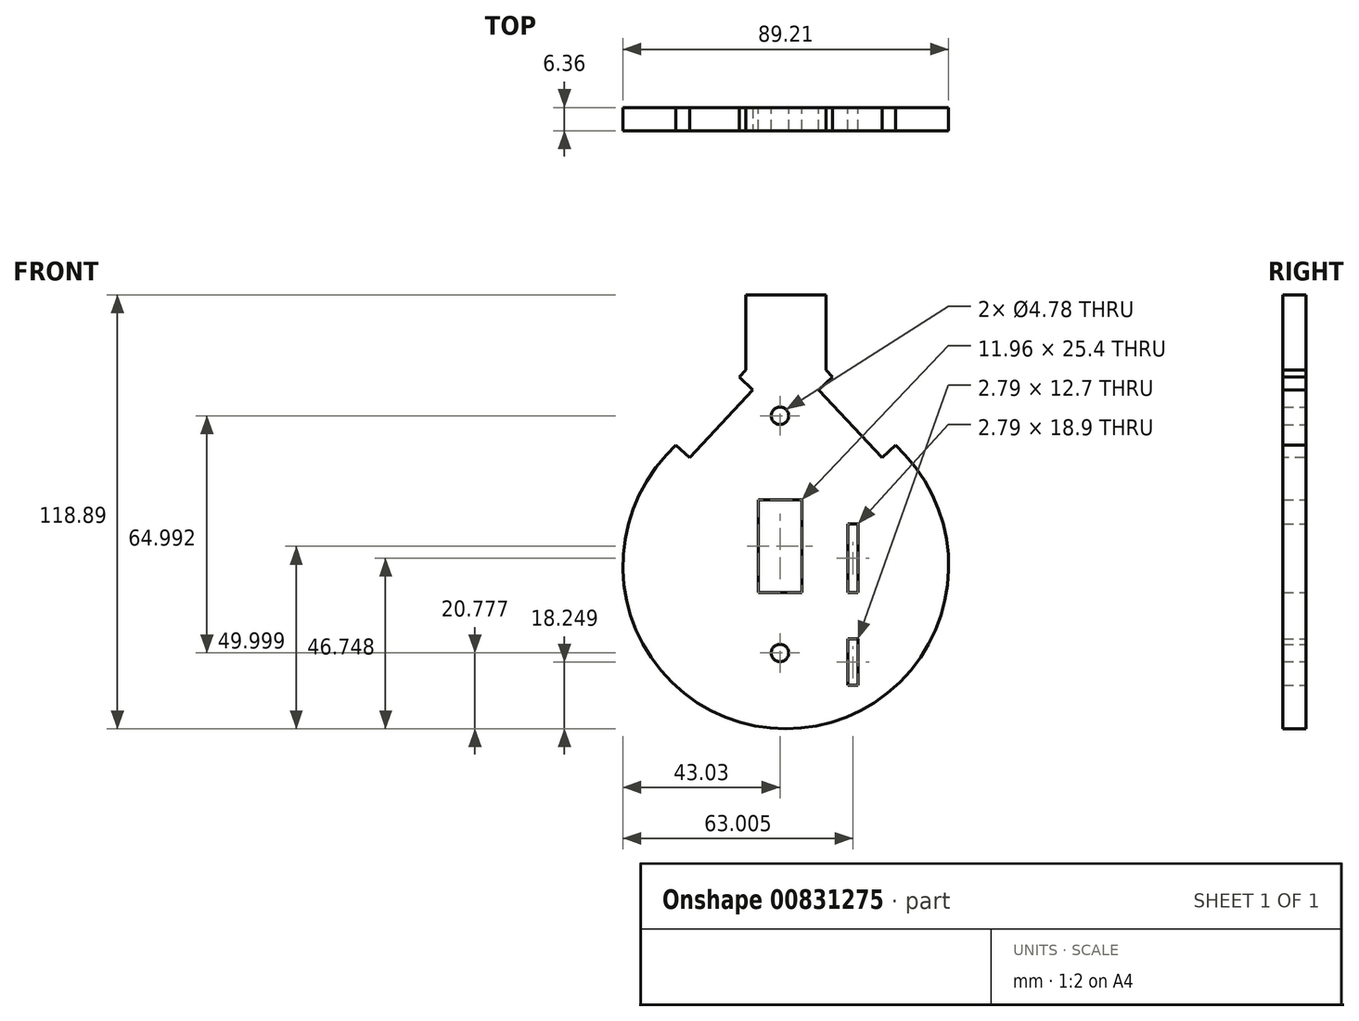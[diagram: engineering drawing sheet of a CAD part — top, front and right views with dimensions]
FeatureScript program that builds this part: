
annotation { "Feature Type Name" : "Feature", "Feature Type Description" : "" }
export const myFeature = defineFeature(function(context is Context, id is Id, definition is map)
    precondition{}
    {
        {
            var Q0;
            Q0=qCreatedBy(makeId("Front.planeOp"),FACE);
            var sketch = newSketch(context, id + "F0", { "sketchPlane" : qUnion([Q0])});
            skArc(sketch, "E0", {"start": v(-31.05, 0) * mm, "mid": v(1.57, -75.03) * mm, "end": v(34.2, 0) * mm});
            skLineSegment(sketch, "E1", {"start": v(-31.05, 0) * mm, "end": v(-9.4, 23.22) * mm});
            skLineSegment(sketch, "E2", {"start": v(34.2, 0) * mm, "end": v(12.55, 23.22) * mm});
            skLineSegment(sketch, "E3", {"start": v(-9.4, 23.22) * mm, "end": v(-9.4, 43.86) * mm});
            skLineSegment(sketch, "E4", {"start": v(12.55, 23.22) * mm, "end": v(12.55, 43.86) * mm});
            skLineSegment(sketch, "E5", {"start": v(-9.4, 43.86) * mm, "end": v(12.55, 43.86) * mm});
            skCircle(sketch, "E6", {"center": v(0, 10.74) * mm, "radius": 2.39 * mm});
            skCircle(sketch, "E7", {"center": v(0, -54.25) * mm, "radius": 2.39 * mm});
            skLineSegment(sketch, "E8.bottom", {"start": v(5.98, -12.33) * mm, "end": v(-5.98, -12.33) * mm});
            skLineSegment(sketch, "E8.top", {"start": v(5.98, -37.73) * mm, "end": v(-5.98, -37.73) * mm});
            skLineSegment(sketch, "E8.left", {"start": v(5.98, -12.33) * mm, "end": v(5.98, -37.73) * mm});
            skLineSegment(sketch, "E8.right", {"start": v(-5.98, -12.33) * mm, "end": v(-5.98, -37.73) * mm});
            skPoint(sketch, "E8.middle", {"position": v(0, -25.03) * mm});
            skLineSegment(sketch, "E9.bottom", {"start": v(18.58, -18.83) * mm, "end": v(21.37, -18.83) * mm});
            skLineSegment(sketch, "E9.top", {"start": v(18.58, -37.73) * mm, "end": v(21.37, -37.73) * mm});
            skLineSegment(sketch, "E9.left", {"start": v(18.58, -18.83) * mm, "end": v(18.58, -37.73) * mm});
            skLineSegment(sketch, "E9.right", {"start": v(21.37, -18.83) * mm, "end": v(21.37, -37.73) * mm});
            skLineSegment(sketch, "E10.bottom", {"start": v(21.37, -50.43) * mm, "end": v(18.58, -50.43) * mm});
            skLineSegment(sketch, "E10.top", {"start": v(21.37, -63.13) * mm, "end": v(18.58, -63.13) * mm});
            skLineSegment(sketch, "E10.left", {"start": v(21.37, -50.43) * mm, "end": v(21.37, -63.13) * mm});
            skLineSegment(sketch, "E10.right", {"start": v(18.58, -50.43) * mm, "end": v(18.58, -63.13) * mm});
            skPoint(sketch, "E10.middle", {"position": v(19.98, -56.78) * mm});
            skSolve(sketch);
        }
        {
            var Q0;
            Q0=makeQuery(id+"F0.imprint","IMPRINT",FACE,{"disambiguationData":[TD([[makeQuery(id+"F0.imprint","IMPRINT",EDGE,{"derivedFrom":sQuery(id+"F0.wireOp",EDGE,"E0")}),1.0]])]});
            extrude(context, id + "F1", {"entities" : qUnion([Q0]), "endBound" : BoundingType.SYMMETRIC, "depth" : 6.35 * mm, "offsetDistance" : 25.4 * mm});
        }
        {
            var Q0;
            Q0=makeQuery(id+"F1.opExtrude","SWEPT_FACE",FACE,{"disambiguationData":[OSD([sQuery(id+"F0.wireOp",EDGE,"E1")])]});
            cPlane(context, id + "F2", {"entities" : qUnion([Q0]), "cplaneType" : CPlaneType.OFFSET, "offset" : 0 * mm, "width" : 152.4 * mm, "height" : 152.4 * mm});
        }
        {
            var Q0;
            Q0=qCreatedBy(id+"F2.planeOp",FACE);
            var sketch = newSketch(context, id + "F3", { "sketchPlane" : qUnion([Q0])});
            skLineSegment(sketch, "E11.bottom", {"start": v(-3.17, 7.97) * mm, "end": v(3.18, 7.97) * mm});
            skLineSegment(sketch, "E11.top", {"start": v(-3.18, -17.43) * mm, "end": v(3.17, -17.43) * mm});
            skLineSegment(sketch, "E11.left", {"start": v(-3.17, 7.97) * mm, "end": v(-3.18, -17.43) * mm});
            skLineSegment(sketch, "E11.right", {"start": v(3.18, 7.97) * mm, "end": v(3.17, -17.43) * mm});
            skPoint(sketch, "E11.middle", {"position": v(0, -4.73) * mm});
            skSolve(sketch);
        }
        {
            var Q0;
            Q0=makeQuery(id+"F3.imprint","IMPRINT",FACE,{"disambiguationData":[TD([[makeQuery(id+"F3.imprint","IMPRINT",EDGE,{"derivedFrom":sQuery(id+"F3.wireOp",EDGE,"E11.bottom")}),-1.0]])]});
            extrude(context, id + "F4", {"entities" : qUnion([Q0]), "operationType" : NewBodyOperationType.REMOVE, "oppositeDirection" : true, "depth" : 5.08 * mm, "offsetDistance" : 25.4 * mm});
        }
        {
            var Q0;
            Q0=makeQuery(id+"F1.opExtrude","SWEPT_FACE",FACE,{"disambiguationData":[OSD([sQuery(id+"F0.wireOp",EDGE,"E2")])]});
            cPlane(context, id + "F5", {"entities" : qUnion([Q0]), "cplaneType" : CPlaneType.OFFSET, "offset" : 0 * mm, "width" : 152.4 * mm, "height" : 152.4 * mm});
        }
        {
            var Q0;
            Q0=qCreatedBy(id+"F5.planeOp",FACE);
            var sketch = newSketch(context, id + "F6", { "sketchPlane" : qUnion([Q0])});
            skLineSegment(sketch, "E12.bottom", {"start": v(-3.17, 5.82) * mm, "end": v(3.18, 5.82) * mm});
            skLineSegment(sketch, "E12.top", {"start": v(-3.17, -19.58) * mm, "end": v(3.18, -19.58) * mm});
            skLineSegment(sketch, "E12.left", {"start": v(-3.17, 5.82) * mm, "end": v(-3.17, -19.58) * mm});
            skLineSegment(sketch, "E12.right", {"start": v(3.18, 5.82) * mm, "end": v(3.18, -19.58) * mm});
            skPoint(sketch, "E12.middle", {"position": v(0, -6.88) * mm});
            skSolve(sketch);
        }
        {
            var Q0;
            Q0=makeQuery(id+"F6.imprint","IMPRINT",FACE,{"disambiguationData":[TD([[makeQuery(id+"F6.imprint","IMPRINT",EDGE,{"derivedFrom":sQuery(id+"F6.wireOp",EDGE,"E12.bottom")}),-1.0]])]});
            extrude(context, id + "F7", {"entities" : qUnion([Q0]), "operationType" : NewBodyOperationType.REMOVE, "oppositeDirection" : true, "depth" : 5.08 * mm, "offsetDistance" : 25.4 * mm});
        }
    });
